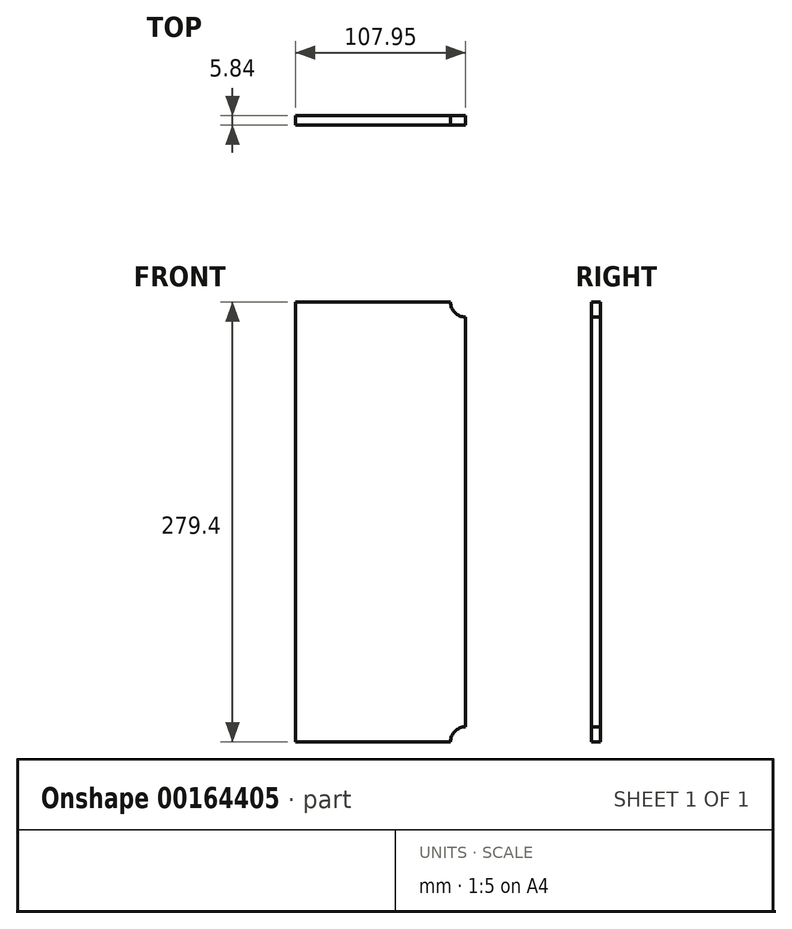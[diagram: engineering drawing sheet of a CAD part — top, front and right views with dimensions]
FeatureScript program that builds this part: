
annotation { "Feature Type Name" : "Feature", "Feature Type Description" : "" }
export const myFeature = defineFeature(function(context is Context, id is Id, definition is map)
    precondition{}
    {
        {
            var Q0;
            Q0=qCreatedBy(makeId("Front.planeOp"),FACE);
            var sketch = newSketch(context, id + "F0", { "sketchPlane" : qUnion([Q0])});
            skLineSegment(sketch, "E0.bottom", {"start": v(0, 279.4) * mm, "end": v(98.42, 279.4) * mm});
            skLineSegment(sketch, "E0.top", {"start": v(0, 0) * mm, "end": v(98.43, 0) * mm});
            skLineSegment(sketch, "E0.left", {"start": v(0, 279.4) * mm, "end": v(0, 0) * mm});
            skLineSegment(sketch, "E0.right", {"start": v(107.95, 269.88) * mm, "end": v(107.95, 9.53) * mm});
            skArc(sketch, "E1", {"start": v(98.42, 279.4) * mm, "mid": v(101.21, 272.66) * mm, "end": v(107.95, 269.88) * mm});
            skArc(sketch, "E2", {"start": v(107.95, 9.52) * mm, "mid": v(101.21, 6.74) * mm, "end": v(98.43, 0) * mm});
            skSolve(sketch);
        }
        {
            var Q0;
            Q0 = qSketchRegion(id + "F0", true);
            extrude(context, id + "F1", {"entities" : qUnion([Q0]), "depth" : 5.84 * mm});
        }
    });
